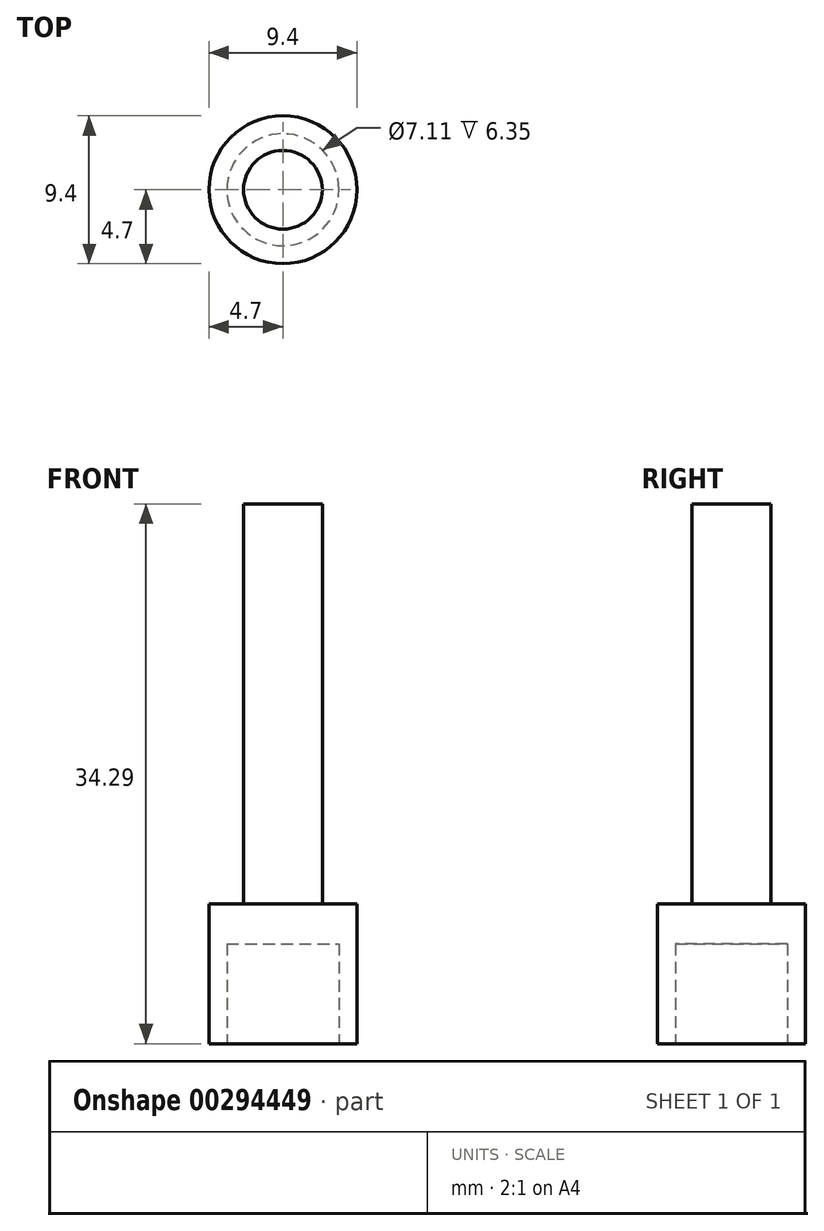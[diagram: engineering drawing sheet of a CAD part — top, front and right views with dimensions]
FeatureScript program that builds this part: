
annotation { "Feature Type Name" : "Feature", "Feature Type Description" : "" }
export const myFeature = defineFeature(function(context is Context, id is Id, definition is map)
    precondition{}
    {
        {
            var Q0;
            Q0=qCreatedBy(makeId("Top.planeOp"),FACE);
            var sketch = newSketch(context, id + "F0", { "sketchPlane" : qUnion([Q0])});
            skCircle(sketch, "E0", {"center": v(0, 0) * mm, "radius": 4.7 * mm});
            skSolve(sketch);
        }
        {
            var Q0;
            Q0=makeQuery(id+"F0.imprint","IMPRINT",FACE,{"disambiguationData":[TD([[makeQuery(id+"F0.imprint","IMPRINT",EDGE,{"derivedFrom":sQuery(id+"F0.wireOp",EDGE,"E0")}),1.0]])]});
            extrude(context, id + "F1", {"entities" : qUnion([Q0]), "depth" : 8.9 * mm});
        }
        {
            var Q0;
            Q0=makeQuery(id+"F1.opExtrude","CAP_FACE",FACE,{"disambiguationData":[OSD([sQuery(id+"F0.wireOp",EDGE,"E0")])],"isStart":false});
            var sketch = newSketch(context, id + "F2", { "sketchPlane" : qUnion([Q0])});
            skCircle(sketch, "E1", {"center": v(0, 0) * mm, "radius": 2.5 * mm});
            skSolve(sketch);
        }
        {
            var Q0;
            Q0=makeQuery(id+"F2.imprint","IMPRINT",FACE,{"disambiguationData":[TD([[makeQuery(id+"F2.imprint","IMPRINT",EDGE,{"derivedFrom":sQuery(id+"F2.wireOp",EDGE,"E1")}),1.0]])]});
            extrude(context, id + "F3", {"entities" : qUnion([Q0]), "operationType" : NewBodyOperationType.ADD, "depth" : 25.4 * mm});
        }
        {
            var Q0;
            Q0=makeQuery(id+"F1.opExtrude","CAP_FACE",FACE,{"disambiguationData":[OSD([sQuery(id+"F0.wireOp",EDGE,"E0")])],"isStart":true});
            var sketch = newSketch(context, id + "F4", { "sketchPlane" : qUnion([Q0])});
            skCircle(sketch, "E2", {"center": v(0, 0) * mm, "radius": 3.56 * mm});
            skSolve(sketch);
        }
        {
            var Q0;
            {var subQ0=sQuery(id+"F4.wireOp",EDGE,"gVh9WAw1-zjv3-rOam-4ilL-nljnmY5gptwo");Q0=makeQuery(id+"F4.imprint","IMPRINT",FACE,{"disambiguationData":[TD([[makeQuery(id+"F4.imprint","IMPRINT",EDGE,{"derivedFrom":subQ0}),1.0]])]});}
            var Q1;
            Q1=makeQuery(id+"F4.imprint","IMPRINT",FACE,{"disambiguationData":[TD([[makeQuery(id+"F4.imprint","IMPRINT",EDGE,{"derivedFrom":sQuery(id+"F4.wireOp",EDGE,"E2")}),1.0]])]});
            extrude(context, id + "F5", {"entities" : qUnion([Q0, Q1]), "operationType" : NewBodyOperationType.REMOVE, "oppositeDirection" : true, "depth" : 6.35 * mm});
        }
    });
